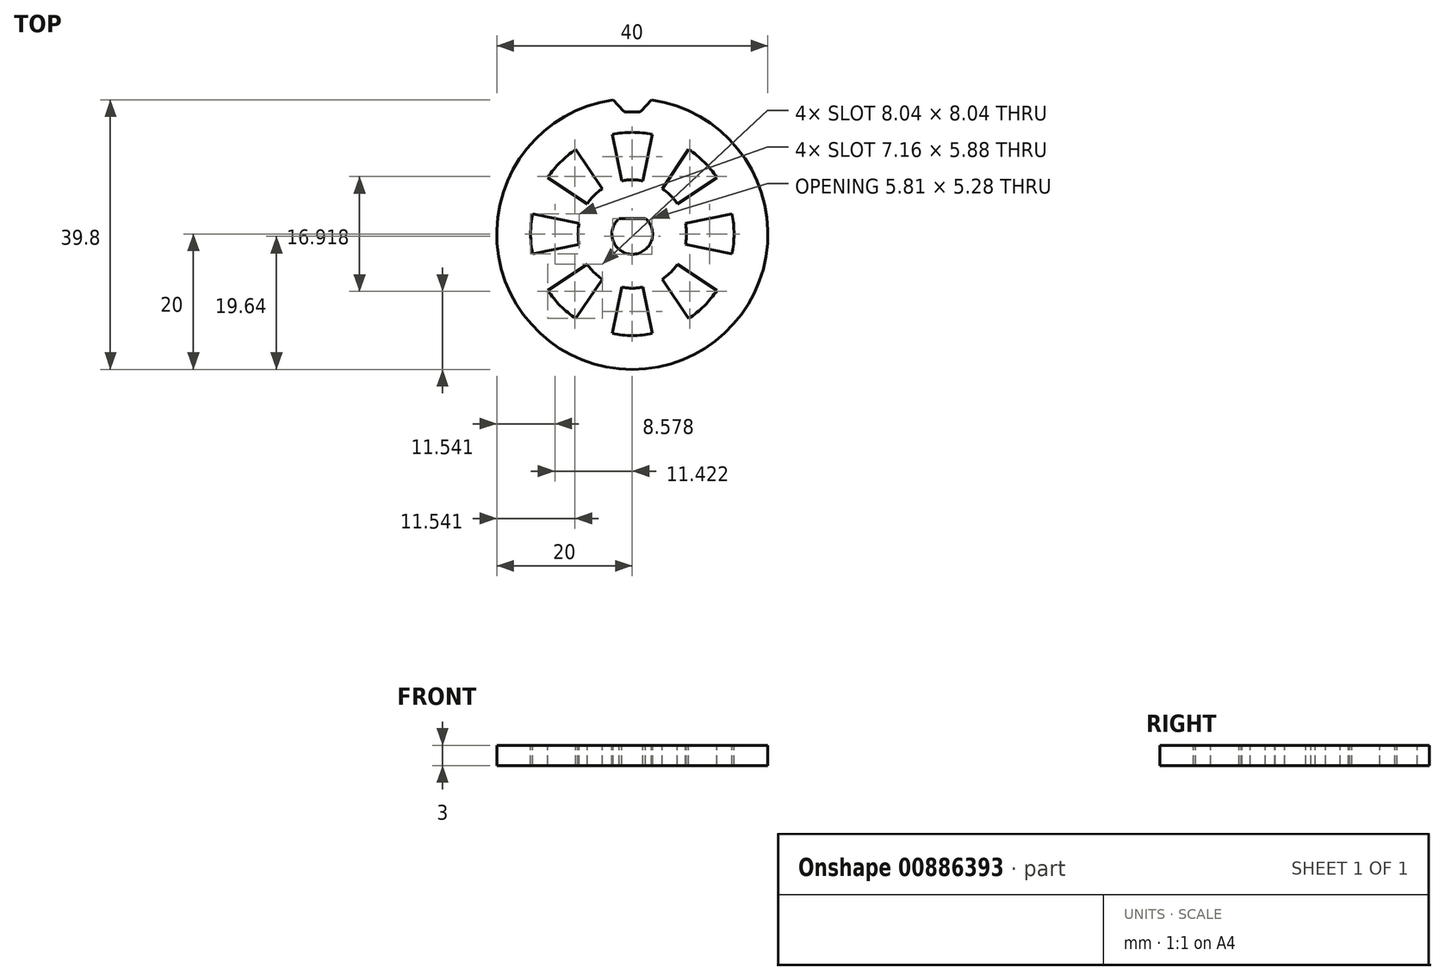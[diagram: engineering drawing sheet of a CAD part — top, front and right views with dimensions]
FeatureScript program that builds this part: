
annotation { "Feature Type Name" : "Feature", "Feature Type Description" : "" }
export const myFeature = defineFeature(function(context is Context, id is Id, definition is map)
    precondition{}
    {
        {
            var Q0;
            Q0=qCreatedBy(makeId("Top.planeOp"),FACE);
            var sketch = newSketch(context, id + "F0", { "sketchPlane" : qUnion([Q0])});
            skCircle(sketch, "E0", {"center": v(0, 0) * mm, "radius": 20 * mm});
            skSolve(sketch);
        }
        {
            var Q0;
            Q0=qSketchRegion(id+"F0",true);
            extrude(context, id + "F1", {"entities" : qUnion([Q0]), "depth" : 3 * mm, "offsetDistance" : 25 * mm, "symmetric" : true});
        }
        {
            var Q0;
            Q0=makeQuery(id+"F0.imprint","IMPRINT",FACE,{"disambiguationData":[TD([[makeQuery(id+"F0.imprint","IMPRINT",EDGE,{"derivedFrom":sQuery(id+"F0.wireOp",EDGE,"E0")}),1.0]])]});
            var sketch = newSketch(context, id + "F2", { "sketchPlane" : qUnion([Q0])});
            skCircle(sketch, "E1", {"center": v(0, 0) * mm, "radius": 18 * mm, "construction": true});
            skSolve(sketch);
        }
        {
            var Q0;
            Q0=makeQuery(id+"F1.opExtrude","CAP_FACE",FACE,{"disambiguationData":[OSD([sQuery(id+"F0.wireOp",EDGE,"E0")])],"isStart":false});
            var sketch = newSketch(context, id + "F3", { "sketchPlane" : qUnion([Q0]), "disableImprinting" : false});
            skLineSegment(sketch, "E2", {"start": v(3, 20) * mm, "end": v(1.13, 18) * mm});
            skLineSegment(sketch, "E3.MirrorCS", {"start": v(-3, 20) * mm, "end": v(-1.13, 18) * mm});
            skLineSegment(sketch, "E4", {"start": v(-3, 20) * mm, "end": v(3, 20) * mm});
            skLineSegment(sketch, "E5", {"start": v(-1.13, 18) * mm, "end": v(1.13, 18) * mm});
            skLineSegment(sketch, "E6", {"start": v(0, 20) * mm, "end": v(0, 18) * mm, "construction": true});
            skLineSegment(sketch, "E7", {"start": v(0, 18) * mm, "end": v(0, 0) * mm, "construction": true});
            skSolve(sketch);
        }
        {
            var Q0;
            {var subQ4=sQuery(id+"F3.wireOp",EDGE,"E5");Q0=makeQuery(id+"F3.imprint","IMPRINT",FACE,{"disambiguationData":[TD([[makeQuery(id+"F3.imprint","IMPRINT",EDGE,{"derivedFrom":subQ4}),1.0]])]});}
            extrude(context, id + "F4", {"entities" : qUnion([Q0]), "operationType" : NewBodyOperationType.REMOVE, "flatOperationType" : FlatOperationType.REMOVE, "oppositeDirection" : true, "depth" : 25 * mm, "offsetDistance" : 25 * mm, "domain" : OperationDomain.MODEL});
        }
        {
            var Q0;
            Q0=makeQuery(id+"F4.boolean.opBoolean","COPY",EDGE,{"derivedFrom":makeQuery(id+"F4.opExtrude","SWEPT_EDGE",EDGE,{"disambiguationData":[OSD([sQuery(id+"F3.wireOp",EDGE,"ey9PAVy1-jMS7-cx7V-Ta8g-zFfhROlCruSM"),sQuery(id+"F3.wireOp",EDGE,"E2")])]})});
            var Q1;
            Q1=makeQuery(id+"F4.boolean.opBoolean","COPY",EDGE,{"derivedFrom":makeQuery(id+"F4.opExtrude","SWEPT_EDGE",EDGE,{"disambiguationData":[OSD([sQuery(id+"F3.wireOp",EDGE,"E3.MirrorCS"),sQuery(id+"F3.wireOp",EDGE,"29845d97-1c8b-497f-aa78-0992a50d87be0.MirrorCS")])]})});
            var Q2;
            Q2=makeQuery(id+"F4.boolean.opBoolean","COPY",EDGE,{"derivedFrom":makeQuery(id+"F4.opExtrude","SWEPT_EDGE",EDGE,{"disambiguationData":[OSD([sQuery(id+"F0.wireOp",EDGE,"E0"),sQuery(id+"F3.wireOp",EDGE,"E2")])]})});
            var Q3;
            Q3=makeQuery(id+"F4.boolean.opBoolean","COPY",EDGE,{"derivedFrom":makeQuery(id+"F4.opExtrude","SWEPT_EDGE",EDGE,{"disambiguationData":[OSD([sQuery(id+"F0.wireOp",EDGE,"E0"),sQuery(id+"F3.wireOp",EDGE,"E3.MirrorCS")])]})});
            fillet(context, id + "F5", {"entities" : qUnion([Q0, Q1, Q2, Q3]), "radius" : .5 * mm, "tangentPropagation" : true, "allowEdgeOverflow" : false});
        }
        {
            var Q0;
            Q0=makeQuery(id+"F1.opExtrude","CAP_FACE",FACE,{"disambiguationData":[OSD([sQuery(id+"F0.wireOp",EDGE,"E0")])],"isStart":false});
            var sketch = newSketch(context, id + "F6", { "sketchPlane" : qUnion([Q0]), "disableImprinting" : false});
            skCircle(sketch, "E8", {"center": v(0, 0) * mm, "radius": 3 * mm});
            skLineSegment(sketch, "E9", {"start": v(1.95, 2.28) * mm, "end": v(-1.95, 2.28) * mm});
            skLineSegment(sketch, "E10", {"start": v(0, 2.28) * mm, "end": v(0, 0) * mm, "construction": true});
            skSolve(sketch);
        }
        {
            var Q0;
            {var subQ0=sQuery(id+"F6.wireOp",EDGE,"E9");var subQ4=makeQuery(id+"F6.imprint","IMPRINT",VERTEX,{"derivedFrom":subQ0});Q0=makeQuery(id+"F6.imprint","IMPRINT",FACE,{"disambiguationData":[TD([[makeQuery(id+"F6.imprint","IMPRINT",EDGE,{"disambiguationData":[TD([[subQ4,1.0]])],"derivedFrom":subQ0}),1.0]])]});}
            extrude(context, id + "F7", {"entities" : qUnion([Q0]), "operationType" : NewBodyOperationType.REMOVE, "oppositeDirection" : true, "depth" : 25 * mm, "offsetDistance" : 25 * mm});
        }
        {
            var Q0;
            Q0=makeQuery(id+"F1.opExtrude","CAP_FACE",FACE,{"disambiguationData":[OSD([sQuery(id+"F0.wireOp",EDGE,"E0")])],"isStart":false});
            var sketch = newSketch(context, id + "F8", { "sketchPlane" : qUnion([Q0]), "disableImprinting" : false});
            skCircle(sketch, "E11", {"center": v(0, 0) * mm, "radius": 8 * mm});
            skCircle(sketch, "E12", {"center": v(0, 0) * mm, "radius": 15 * mm});
            skLineSegment(sketch, "E13", {"start": v(-3, 15) * mm, "end": v(0, 0) * mm});
            skLineSegment(sketch, "E14", {"start": v(3, 15) * mm, "end": v(0, 0) * mm});
            skLineSegment(sketch, "E15", {"start": v(-3, 15) * mm, "end": v(3, 15) * mm});
            skLineSegment(sketch, "E16", {"start": v(0, 0) * mm, "end": v(0, 15) * mm, "construction": true});
            skSolve(sketch);
        }
        {
            var Q0;
            {var subQ0=sQuery(id+"F8.wireOp",EDGE,"E13");var subQ1=sQuery(id+"F8.wireOp",EDGE,"E11");var subQ2=makeQuery(id+"F8.imprint","INTERSECT",VERTEX,{"derivedFrom":[subQ1,subQ0]});Q0=makeQuery(id+"F8.imprint","IMPRINT",FACE,{"disambiguationData":[TD([[makeQuery(id+"F8.imprint","IMPRINT",EDGE,{"disambiguationData":[TD([[subQ2,1.0]])],"derivedFrom":subQ1}),-1.0]])]});}
            extrude(context, id + "F9", {"entities" : qUnion([Q0]), "operationType" : NewBodyOperationType.REMOVE, "oppositeDirection" : true, "depth" : 25 * mm, "offsetDistance" : 25 * mm});
        }
        {
            var Q0;
            Q0=makeQuery(id+"F9.boolean.opBoolean","COPY",FACE,{"derivedFrom":makeQuery(id+"F9.opExtrude","SWEPT_FACE",FACE,{"disambiguationData":[OSD([sQuery(id+"F8.wireOp",EDGE,"E11")])]})});
            var Q1;
            Q1=makeQuery(id+"F9.boolean.opBoolean","COPY",FACE,{"derivedFrom":makeQuery(id+"F9.opExtrude","SWEPT_FACE",FACE,{"disambiguationData":[OSD([sQuery(id+"F8.wireOp",EDGE,"E13")])]})});
            var Q2;
            Q2=makeQuery(id+"F9.boolean.opBoolean","COPY",FACE,{"derivedFrom":makeQuery(id+"F9.opExtrude","SWEPT_FACE",FACE,{"disambiguationData":[OSD([sQuery(id+"F8.wireOp",EDGE,"E12")])]})});
            var Q3;
            Q3=makeQuery(id+"F9.boolean.opBoolean","COPY",FACE,{"derivedFrom":makeQuery(id+"F9.opExtrude","SWEPT_FACE",FACE,{"disambiguationData":[OSD([sQuery(id+"F8.wireOp",EDGE,"E14")])]})});
            var Q4;
            Q4=makeQuery(id+"F7.boolean.opBoolean","COPY",FACE,{"derivedFrom":makeQuery(id+"F7.opExtrude","SWEPT_FACE",FACE,{"disambiguationData":[OSD([sQuery(id+"F6.wireOp",EDGE,"E8")])]})});
            circularPattern(context, id + "F10", {"patternType" : PatternType.FACE, "faces" : qUnion([Q0, Q1, Q2, Q3]), "axis" : qUnion([Q4]), "angle" : 360 * degree, "instanceCount" : 8, "equalSpace" : true, "computeTransformsWithoutBuiltin" : true});
        }
    });
